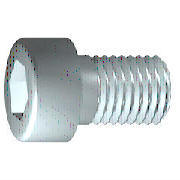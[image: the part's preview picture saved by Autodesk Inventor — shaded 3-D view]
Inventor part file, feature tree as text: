
AUTODESK INVENTOR PART (.ipt)
format: ipt  version: 2016 (Build 200138000, 138)  size: 187,392 bytes
history: native  units: mm (DEFAULTED — no unit token found)
features: sketch x2, other x1, extrude x1, plane x1, fillet x1
ambient origin geometry x7: Origin, YZ Plane, XY Plane, X Axis, Y Axis, Z Axis, Center Point
bodies: Solid1 (feature_tree)
feature tree (6):
  other  "Körper"
  extrude  "Loch"  Depth=3.0mm
  plane  "Work Plane1"
  fillet  "Fillet2"  Radius=3.0mm
  sketch  "Skizze1"  dims[d1=18.75mm d2=0.306825mm d3=3.0mm]
  sketch  "Skizze2"  dims[d4=1.3mm d5=60.0deg d6=3.0mm d7=3.0mm d8=2.886751mm d9=5.5mm d10=90.0deg d11=10.0mm d12=0.0mm d13=18.75mm d14=0.0mm d15=0.306725mm d16=0.306725mm d17=0.3mm d19=0.0mm d26=20.0mm d27=45.0deg d28=0.0mm d29=0.0mm d30=0.1mm]
